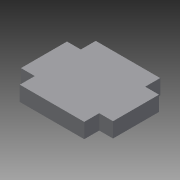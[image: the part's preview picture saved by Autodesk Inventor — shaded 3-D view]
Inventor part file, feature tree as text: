
AUTODESK INVENTOR PART (.ipt)
format: ipt  version: 2013 (Build 170138000, 138)  size: 98,304 bytes
history: native  units: mm
features: other x2, extrude x1, sketch x1
ambient origin geometry x8: Origin, YZ Plane, XZ Plane, XY Plane, X Axis, Y Axis, Z Axis, Center Point
feature tree (4):
  other  "Blocks"
  extrude  "Extrusion4"  Depth=3.0mm
  sketch  "Sketch1"  dims[d0=3.0mm d2=3.0mm d3=0.1mm d7=22.5mm d8=12.4mm d9=4.5mm d10=4.5mm d11=2.0mm d12=2.0mm d34=14.0mm d35=3.25mm d36=20.0mm d37=10.0mm d38=3.25mm d39=0.0mm]
  other  "Block1"
